# Revit family: Door-Sliding-All_Weather-Series_8100-Bi-Parting
name_source: partatom
category: Doors
units: mm (PartAtom-declared; Revit-internal decimal feet)

## family parameters
Always vertical = Yes
Classification Number = 23.30.10.00
Cut with Voids When Loaded = No
Host = Wall
Room Calculation Point = No
Shared = No

## types (1)
- 4 Panel Sliding Door - OXXO
    Analytic Construction = <None>
    Assembly Code = B2030110
    Center Panel Location = 0' - 11 1/4"
    Description = Thermally Broken Stacking Door
    End Panel Offset = 0' - 3"
    Exterior Trim = No
    Exterior Trim Finish = Metal-Aluminum-All_Weather-Standard-White
    Finish = Metal-Aluminum-All_Weather-Standard-White
    Frame Projection Ext. = 0' - 1"
    Frame Projection Int. = 0' - 1"
    Frame Width = 0' - 3"
    Function = Exterior
    Glazing = Glass-All_Weather-OA-Insulated_Glass
    Height = 8' - 0"
    Inset = 0' - 0"
    Interior Trim = No
    Interior Trim Finish = Metal-Aluminum-All_Weather-Standard-White
    Jamb Ext Finish = Metal-Aluminum-All_Weather-Standard-White
    Jamb Extensions = Yes
    Manufacturer = All Weather Architectural Aluminum
    Max Panel Height = 12' - 0"
    Max Panel Width = 6' - 0"
    Max Width = 24' - 0 3/4"
    Min Panel Width = 1' - 8 1/2"
    Min Width = 6' - 10 3/4"
    Model = OXXO
    Number of Panels = 4
    Offset = 0' - 0"
    Opening Width = 7' - 10"
    Operation = Sliding
    Panel Height = 7' - 10 3/4"
    Panel Offset = 0' - 2 31/32"
    Panel Spacing = 0' - 2"
    Panel Thickness = 0' - 2"
    Panel Width = 2' - 1 5/32"
    Product Documentation Link = https://www.allweatheraa.com
    Product Name = Series 8100
    Product Page URL = https://www.allweatheraa.com
    Requested Height = 8' - 0"
    Requested Width = 8' - 0"
    Rough Height = 8' - 0 1/2"
    Rough Width = 8' - 1"
    Thickness = 0' - 4"
    Type Comments = Multi-Panel Sliding Door
    URL = https://www.allweatheraa.com
    Wall Closure = By host
    Width = 8' - 0"

## geometry (parser evidence)
native form markers: Sweep x9
no freeform markers — native parametric forms only
